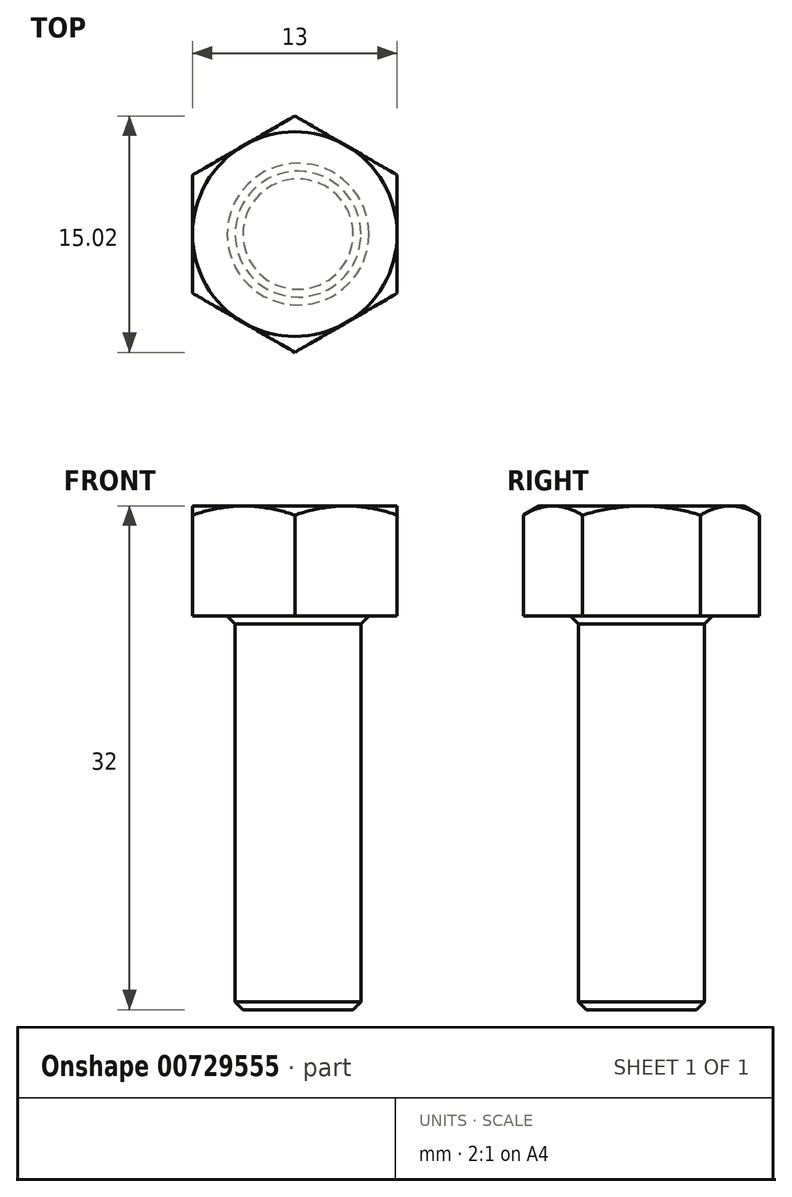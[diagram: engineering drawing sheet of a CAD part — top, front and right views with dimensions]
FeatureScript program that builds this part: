
annotation { "Feature Type Name" : "Feature", "Feature Type Description" : "" }
export const myFeature = defineFeature(function(context is Context, id is Id, definition is map)
    precondition{}
    {
        {
            var Q0;
            Q0=qCreatedBy(makeId("Top.planeOp"),FACE);
            var sketch = newSketch(context, id + "F0", { "sketchPlane" : qUnion([Q0])});
            skCircle(sketch, "E0.cCircle", {"center": v(0, 0) * mm, "radius": 6.5 * mm, "construction": true});
            skLineSegment(sketch, "E0.0", {"start": v(6.5, -3.75) * mm, "end": v(0, -7.5) * mm});
            skLineSegment(sketch, "E0.1", {"start": v(0, -7.5) * mm, "end": v(-6.5, -3.75) * mm});
            skLineSegment(sketch, "E0.2", {"start": v(-6.5, -3.75) * mm, "end": v(-6.5, 3.75) * mm});
            skLineSegment(sketch, "E0.3", {"start": v(-6.5, 3.75) * mm, "end": v(0, 7.5) * mm});
            skLineSegment(sketch, "E0.4", {"start": v(0, 7.5) * mm, "end": v(6.5, 3.75) * mm});
            skLineSegment(sketch, "E0.5", {"start": v(6.5, 3.75) * mm, "end": v(6.5, -3.75) * mm});
            skPoint(sketch, "E0.0.midPoint", {"position": v(3.25, -5.63) * mm});
            skCircle(sketch, "E1", {"center": v(0, 0) * mm, "radius": 4 * mm});
            skSolve(sketch);
        }
        {
            var Q0;
            Q0 = qSketchRegion(id + "F0", true);
            var Q1;
            Q1=makeQuery(id+"F0.imprint","IMPRINT",FACE,{"disambiguationData":[TD([[makeQuery(id+"F0.imprint","IMPRINT",EDGE,{"derivedFrom":sQuery(id+"F0.wireOp",EDGE,"E1")}),1.0]])]});
            extrude(context, id + "F1", {"entities" : qUnion([Q0, Q1]), "depth" : 7 * mm, "offsetDistance" : 25 * mm});
        }
        {
            var Q0;
            Q0=qCreatedBy(makeId("Top.planeOp"),FACE);
            var sketch = newSketch(context, id + "F2", { "sketchPlane" : qUnion([Q0])});
            skCircle(sketch, "E2", {"center": v(0.2, 0) * mm, "radius": 4 * mm});
            skSolve(sketch);
        }
        {
            var Q0;
            Q0 = qSketchRegion(id + "F2", true);
            var Q1;
            Q1=makeQuery(id+"F2.imprint","IMPRINT",FACE,{"disambiguationData":[TD([[makeQuery(id+"F2.imprint","IMPRINT",EDGE,{"derivedFrom":sQuery(id+"F2.wireOp",EDGE,"E2")}),1.0]])]});
            extrude(context, id + "F3", {"entities" : qUnion([Q0, Q1]), "operationType" : NewBodyOperationType.ADD, "oppositeDirection" : true, "depth" : 25 * mm, "offsetDistance" : 25 * mm});
        }
        {
            var Q0;
            Q0=makeQuery(id+"F3.opExtrude","SWEPT_FACE",FACE,{"disambiguationData":[OSD([sQuery(id+"F2.wireOp",EDGE,"E2")])]});
            var Q1;
            Q1=makeQuery(id+"F3.opExtrude","CAP_FACE",FACE,{"disambiguationData":[OSD([sQuery(id+"F2.wireOp",EDGE,"E2")])],"isStart":false});
            chamfer(context, id + "F4", {"entities" : qUnion([Q0, Q1]), "width" : 0.5 * mm, "tangentPropagation" : true});
        }
        {
            var Q0;
            Q0=qCreatedBy(makeId("Front.planeOp"),FACE);
            var sketch = newSketch(context, id + "F5", { "sketchPlane" : qUnion([Q0])});
            skLineSegment(sketch, "E3", {"start": v(0, 7.96) * mm, "end": v(0, 0) * mm, "construction": true});
            skLineSegment(sketch, "E4", {"start": v(0, 0) * mm, "end": v(0, 7.96) * mm, "construction": true});
            skLineSegment(sketch, "E5", {"start": v(6.5, 7) * mm, "end": v(13.28, 7) * mm});
            skLineSegment(sketch, "E6", {"start": v(13.28, 7) * mm, "end": v(13.28, 3.09) * mm});
            skLineSegment(sketch, "E7", {"start": v(13.28, 3.09) * mm, "end": v(6.5, 7) * mm});
            skSolve(sketch);
        }
        {
            var Q0;
            Q0 = qSketchRegion(id + "F5", true);
            var Q1;
            Q1=sQuery(id+"F5.wireOp",EDGE,"E3");
            revolve(context, id + "F6", {"operationType" : NewBodyOperationType.REMOVE, "surfaceOperationType" : NewSurfaceOperationType.NEW, "entities" : qUnion([Q0]), "axis" : qUnion([Q1]), "revolveType" : RevolveType.FULL, "oppositeDirection" : true});
        }
    });
